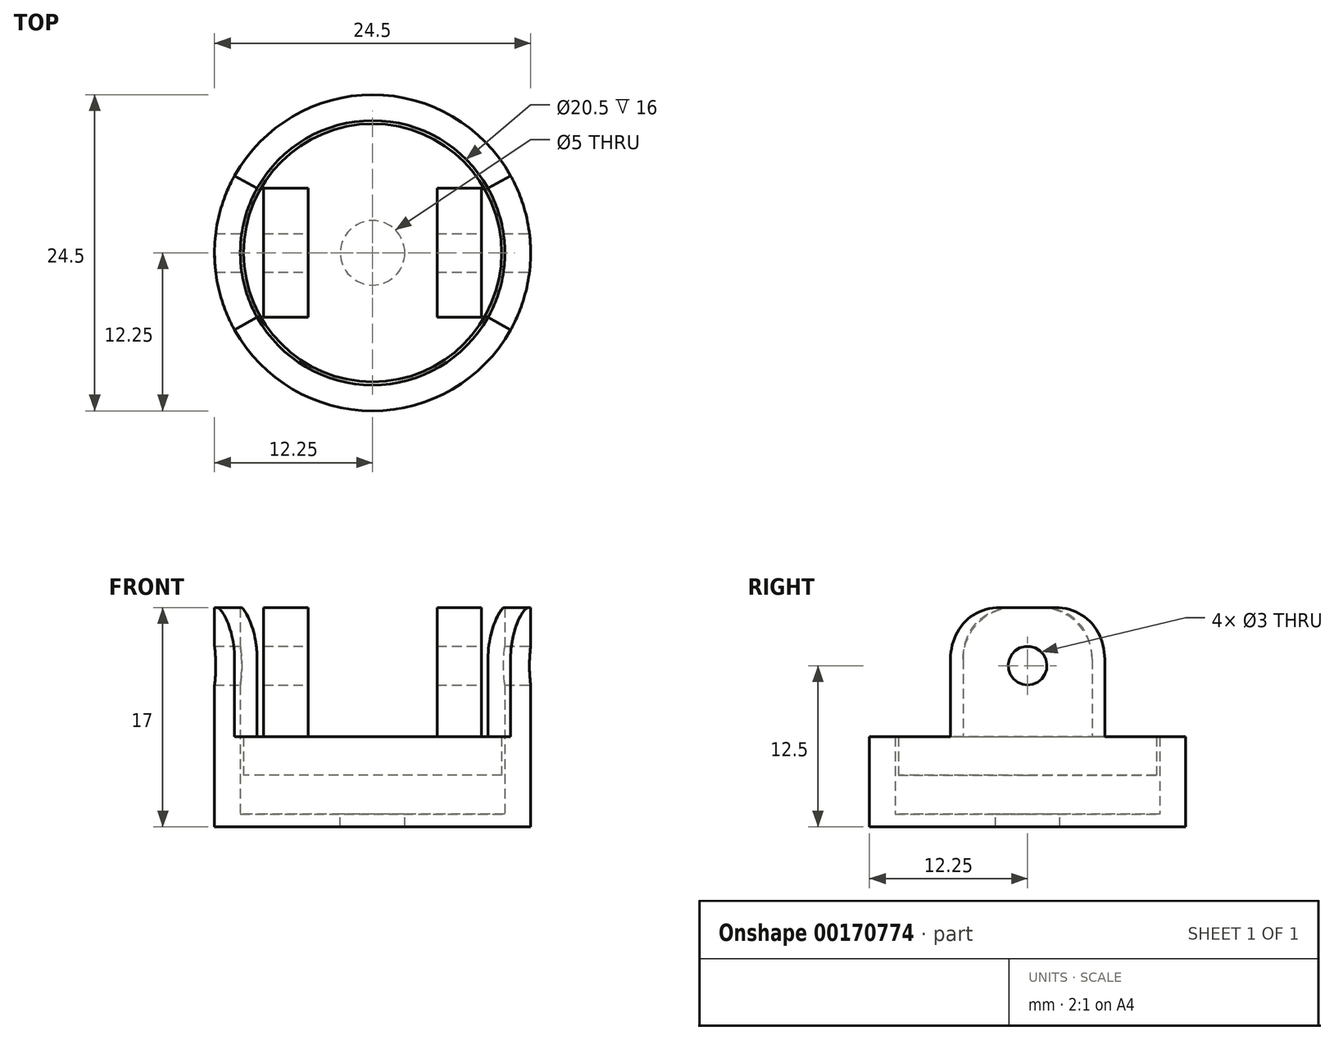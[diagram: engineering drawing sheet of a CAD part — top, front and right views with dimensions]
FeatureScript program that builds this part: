
annotation { "Feature Type Name" : "Feature", "Feature Type Description" : "" }
export const myFeature = defineFeature(function(context is Context, id is Id, definition is map)
    precondition{}
    {
        {
            var Q0;
            Q0=qCreatedBy(makeId("Top.planeOp"),FACE);
            var sketch = newSketch(context, id + "F0", { "sketchPlane" : qUnion([Q0])});
            skCircle(sketch, "E0", {"center": v(0, 0) * mm, "radius": 10.25 * mm});
            skCircle(sketch, "E1", {"center": v(0, 0) * mm, "radius": 12.25 * mm});
            skCircle(sketch, "E2", {"center": v(0, 0) * mm, "radius": 10 * mm});
            skSolve(sketch);
        }
        {
            var Q0;
            Q0=makeQuery(id+"F0.imprint","IMPRINT",FACE,{"disambiguationData":[TD([[makeQuery(id+"F0.imprint","IMPRINT",EDGE,{"derivedFrom":sQuery(id+"F0.wireOp",EDGE,"E2")}),1.0]])]});
            extrude(context, id + "F1", {"entities" : qUnion([Q0]), "depth" : 3 * mm, "offsetDistance" : 25 * mm});
        }
        {
            var Q0;
            Q0=makeQuery(id+"F0.imprint","IMPRINT",FACE,{"disambiguationData":[TD([[makeQuery(id+"F0.imprint","IMPRINT",EDGE,{"derivedFrom":sQuery(id+"F0.wireOp",EDGE,"E0")}),-1.0]])]});
            extrude(context, id + "F2", {"entities" : qUnion([Q0]), "depth" : 3 * mm, "offsetDistance" : 25 * mm, "hasSecondDirection" : true, "secondDirectionOppositeDirection" : true, "secondDirectionDepth" : 4 * mm});
        }
        {
            var Q0;
            Q0=makeQuery(id+"F0.imprint","IMPRINT",FACE,{"disambiguationData":[TD([[makeQuery(id+"F0.imprint","IMPRINT",EDGE,{"derivedFrom":sQuery(id+"F0.wireOp",EDGE,"E0")}),1.0]])]});
            var Q1;
            Q1=makeQuery(id+"F0.imprint","IMPRINT",FACE,{"disambiguationData":[TD([[makeQuery(id+"F0.imprint","IMPRINT",EDGE,{"derivedFrom":sQuery(id+"F0.wireOp",EDGE,"E2")}),1.0]])]});
            extrude(context, id + "F3", {"entities" : qUnion([Q0, Q1]), "operationType" : NewBodyOperationType.ADD, "oppositeDirection" : true, "depth" : 4 * mm, "offsetDistance" : 25 * mm, "hasSecondDirection" : true, "secondDirectionOppositeDirection" : false, "secondDirectionDepth" : -3 * mm});
        }
        {
            var Q0;
            Q0=makeQuery(id+"F2.opExtrude","CAP_FACE",FACE,{"disambiguationData":[OSD([sQuery(id+"F0.wireOp",EDGE,"E0"),sQuery(id+"F0.wireOp",EDGE,"E1")])],"isStart":false});
            var sketch = newSketch(context, id + "F4", { "sketchPlane" : qUnion([Q0])});
            skArc(sketch, "E3", {"start": v(-10.25, 0) * mm, "mid": v(-9.92, 2.58) * mm, "end": v(-8.95, 5) * mm});
            skArc(sketch, "E4", {"start": v(-12.25, 0) * mm, "mid": v(-11.85, 3.09) * mm, "end": v(-10.7, 5.98) * mm});
            skLineSegment(sketch, "E5", {"start": v(-10.7, 5.98) * mm, "end": v(-8.95, 5) * mm});
            skArc(sketch, "E6.MirrorCS", {"start": v(-12.25, 0) * mm, "mid": v(-11.85, -3.09) * mm, "end": v(-10.7, -5.98) * mm});
            skArc(sketch, "E7.MirrorCS", {"start": v(-10.25, 0) * mm, "mid": v(-9.92, -2.58) * mm, "end": v(-8.95, -5) * mm});
            skLineSegment(sketch, "E8.MirrorCS", {"start": v(-10.7, -5.98) * mm, "end": v(-8.95, -5) * mm});
            skLineSegment(sketch, "E9.MirrorCS", {"start": v(10.7, 5.98) * mm, "end": v(8.95, 5) * mm});
            skArc(sketch, "E10.MirrorCS", {"start": v(10.25, 0) * mm, "mid": v(9.92, -2.58) * mm, "end": v(8.95, -5) * mm});
            skArc(sketch, "E11.MirrorCS", {"start": v(10.25, 0) * mm, "mid": v(9.92, 2.58) * mm, "end": v(8.95, 5) * mm});
            skArc(sketch, "E12.MirrorCS", {"start": v(12.25, 0) * mm, "mid": v(11.85, 3.09) * mm, "end": v(10.7, 5.98) * mm});
            skLineSegment(sketch, "E13.MirrorCS", {"start": v(10.7, -5.98) * mm, "end": v(8.95, -5) * mm});
            skArc(sketch, "E14.MirrorCS", {"start": v(12.25, 0) * mm, "mid": v(11.85, -3.09) * mm, "end": v(10.7, -5.98) * mm});
            skSolve(sketch);
        }
        {
            var Q0;
            Q0 = qSketchRegion(id + "F4", true);
            extrude(context, id + "F5", {"entities" : qUnion([Q0]), "operationType" : NewBodyOperationType.ADD, "depth" : 10 * mm, "offsetDistance" : 25 * mm});
        }
        {
            var Q0;
            Q0=makeQuery(id+"F3.opExtrude","CAP_FACE",FACE,{"disambiguationData":[OSD([sQuery(id+"F0.wireOp",EDGE,"E0")])],"isStart":true});
            var sketch = newSketch(context, id + "F6", { "sketchPlane" : qUnion([Q0])});
            skCircle(sketch, "E15", {"center": v(0, 0) * mm, "radius": 2.5 * mm});
            skSolve(sketch);
        }
        {
            var Q0;
            Q0 = qSketchRegion(id + "F6", true);
            extrude(context, id + "F7", {"entities" : qUnion([Q0]), "operationType" : NewBodyOperationType.REMOVE, "endBound" : BoundingType.THROUGH_ALL, "oppositeDirection" : true, "depth" : 25 * mm, "offsetDistance" : 25 * mm});
        }
        {
            var Q0;
            Q0=makeQuery(id+"F1.opExtrude","CAP_FACE",FACE,{"disambiguationData":[OSD([sQuery(id+"F0.wireOp",EDGE,"E2")])],"isStart":false});
            var sketch = newSketch(context, id + "F8", { "sketchPlane" : qUnion([Q0])});
            skLineSegment(sketch, "E16.bottom", {"start": v(5, -5) * mm, "end": v(8.45, -5) * mm});
            skLineSegment(sketch, "E16.top", {"start": v(5, 5) * mm, "end": v(8.45, 5) * mm});
            skLineSegment(sketch, "E16.left", {"start": v(5, -5) * mm, "end": v(5, 5) * mm});
            skLineSegment(sketch, "E16.right", {"start": v(8.45, -5) * mm, "end": v(8.45, 5) * mm});
            skLineSegment(sketch, "E17.MirrorCS", {"start": v(-8.45, -5) * mm, "end": v(-8.45, 5) * mm});
            skLineSegment(sketch, "E18.MirrorCS", {"start": v(-5, -5) * mm, "end": v(-5, 5) * mm});
            skLineSegment(sketch, "E19.MirrorCS", {"start": v(-5, -5) * mm, "end": v(-8.45, -5) * mm});
            skLineSegment(sketch, "E20.MirrorCS", {"start": v(-5, 5) * mm, "end": v(-8.45, 5) * mm});
            skSolve(sketch);
        }
        {
            var Q0;
            Q0 = qSketchRegion(id + "F8", true);
            var Q1;
            Q1=makeQuery(id+"F5.opExtrude","CAP_FACE",FACE,{"disambiguationData":[OSD([sQuery(id+"F4.wireOp",EDGE,"E3"),sQuery(id+"F4.wireOp",EDGE,"E4"),sQuery(id+"F4.wireOp",EDGE,"E5"),sQuery(id+"F4.wireOp",EDGE,"E6.MirrorCS"),sQuery(id+"F4.wireOp",EDGE,"E7.MirrorCS"),sQuery(id+"F4.wireOp",EDGE,"E8.MirrorCS")])],"isStart":false});
            extrude(context, id + "F9", {"entities" : qUnion([Q0]), "operationType" : NewBodyOperationType.ADD, "endBound" : BoundingType.UP_TO_SURFACE, "depth" : 6 * mm, "endBoundEntityFace" : qUnion([Q1]), "offsetDistance" : 25 * mm});
        }
        {
            var Q0;
            Q0=makeQuery(id+"F5.opExtrude","CAP_EDGE",EDGE,{"disambiguationData":[OSD([sQuery(id+"F4.wireOp",EDGE,"E5")])],"isStart":false});
            var Q1;
            Q1=makeQuery(id+"F5.opExtrude","CAP_EDGE",EDGE,{"disambiguationData":[OSD([sQuery(id+"F4.wireOp",EDGE,"E8.MirrorCS")])],"isStart":false});
            var Q2;
            Q2=makeQuery(id+"F5.opExtrude","CAP_EDGE",EDGE,{"disambiguationData":[OSD([sQuery(id+"F4.wireOp",EDGE,"E13.MirrorCS")])],"isStart":false});
            var Q3;
            Q3=makeQuery(id+"F5.opExtrude","CAP_EDGE",EDGE,{"disambiguationData":[OSD([sQuery(id+"F4.wireOp",EDGE,"E9.MirrorCS")])],"isStart":false});
            var Q4;
            Q4=makeQuery(id+"F9.opExtrude","CAP_EDGE",EDGE,{"disambiguationData":[OSD([sQuery(id+"F8.wireOp",EDGE,"E16.bottom")])],"isStart":false});
            var Q5;
            Q5=makeQuery(id+"F9.opExtrude","CAP_EDGE",EDGE,{"disambiguationData":[OSD([sQuery(id+"F8.wireOp",EDGE,"E19.MirrorCS")])],"isStart":false});
            var Q6;
            Q6=makeQuery(id+"F9.opExtrude","CAP_EDGE",EDGE,{"disambiguationData":[OSD([sQuery(id+"F8.wireOp",EDGE,"E16.top")])],"isStart":false});
            var Q7;
            Q7=makeQuery(id+"F9.opExtrude","CAP_EDGE",EDGE,{"disambiguationData":[OSD([sQuery(id+"F8.wireOp",EDGE,"E20.MirrorCS")])],"isStart":false});
            fillet(context, id + "F10", {"entities" : qUnion([Q0, Q1, Q2, Q3, Q4, Q5, Q6, Q7]), "radius" : 4 * mm, "tangentPropagation" : true, "allowEdgeOverflow" : false});
        }
        {
            var Q0;
            Q0=qCreatedBy(makeId("Right.planeOp"),FACE);
            var sketch = newSketch(context, id + "F11", { "sketchPlane" : qUnion([Q0])});
            skCircle(sketch, "E21", {"center": v(0, 8.5) * mm, "radius": 1.5 * mm});
            skSolve(sketch);
        }
        {
            var Q0;
            Q0 = qSketchRegion(id + "F11", true);
            extrude(context, id + "F12", {"entities" : qUnion([Q0]), "operationType" : NewBodyOperationType.REMOVE, "endBound" : BoundingType.THROUGH_ALL, "oppositeDirection" : true, "depth" : 25 * mm, "offsetDistance" : 25 * mm, "hasSecondDirection" : true, "secondDirectionBound" : BoundingType.THROUGH_ALL, "secondDirectionOppositeDirection" : false, "secondDirectionDepth" : 25 * mm});
        }
    });
